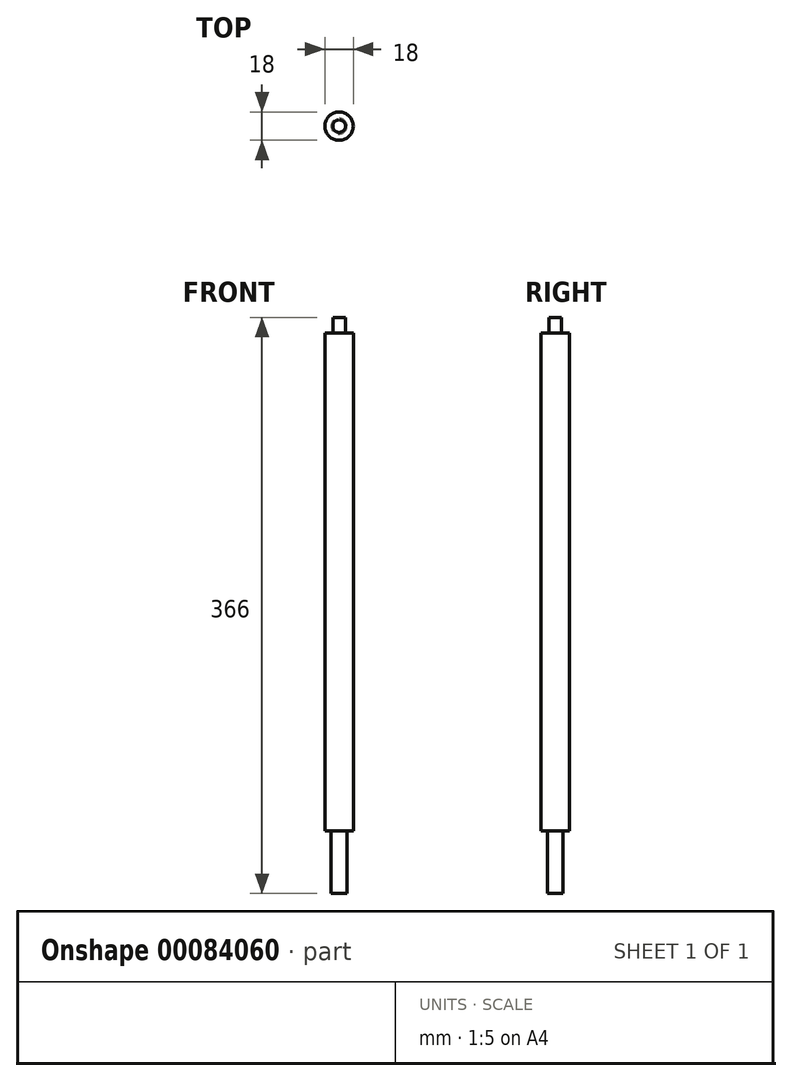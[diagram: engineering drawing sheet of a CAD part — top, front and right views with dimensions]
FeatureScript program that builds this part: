
annotation { "Feature Type Name" : "Feature", "Feature Type Description" : "" }
export const myFeature = defineFeature(function(context is Context, id is Id, definition is map)
    precondition{}
    {
        {
            var Q0;
            Q0=qCreatedBy(makeId("Front.planeOp"),FACE);
            var sketch = newSketch(context, id + "F0", { "sketchPlane" : qUnion([Q0])});
            skLineSegment(sketch, "E0", {"start": v(0, 0) * mm, "end": v(5, 0) * mm});
            skLineSegment(sketch, "E1", {"start": v(5, 0) * mm, "end": v(5, 40) * mm});
            skLineSegment(sketch, "E2", {"start": v(5, 40) * mm, "end": v(9, 40) * mm});
            skLineSegment(sketch, "E3", {"start": v(9, 40) * mm, "end": v(9, 356) * mm});
            skLineSegment(sketch, "E4", {"start": v(9, 356) * mm, "end": v(4, 356) * mm});
            skLineSegment(sketch, "E5", {"start": v(4, 356) * mm, "end": v(4, 366) * mm});
            skLineSegment(sketch, "E6", {"start": v(4, 366) * mm, "end": v(0, 366) * mm});
            skLineSegment(sketch, "E7", {"start": v(0, 366) * mm, "end": v(0, 0) * mm});
            skLineSegment(sketch, "E8", {"start": v(5, 40) * mm, "end": v(0, 40) * mm});
            skLineSegment(sketch, "E9", {"start": v(4, 356) * mm, "end": v(0, 356) * mm});
            skSolve(sketch);
        }
        {
            var Q0;
            Q0=makeQuery(id+"F0.imprint","IMPRINT",FACE,{"disambiguationData":[TD([[makeQuery(id+"F0.imprint","IMPRINT",EDGE,{"derivedFrom":sQuery(id+"F0.wireOp",EDGE,"E5")}),1.0]])]});
            var Q1;
            Q1=makeQuery(id+"F0.imprint","IMPRINT",FACE,{"disambiguationData":[TD([[makeQuery(id+"F0.imprint","IMPRINT",EDGE,{"derivedFrom":sQuery(id+"F0.wireOp",EDGE,"E2")}),1.0]])]});
            var Q2;
            {var subQ0=sQuery(id+"F0.wireOp",EDGE,"E0");Q2=makeQuery(id+"F0.imprint","IMPRINT",FACE,{"disambiguationData":[TD([[makeQuery(id+"F0.imprint","IMPRINT",EDGE,{"derivedFrom":subQ0}),1.0]])]});}
            var Q3;
            Q3=sQuery(id+"F0.wireOp",EDGE,"E7");
            revolve(context, id + "F1", {"entities" : qUnion([Q0, Q1, Q2]), "axis" : qUnion([Q3]), "revolveType" : RevolveType.FULL});
        }
    });
